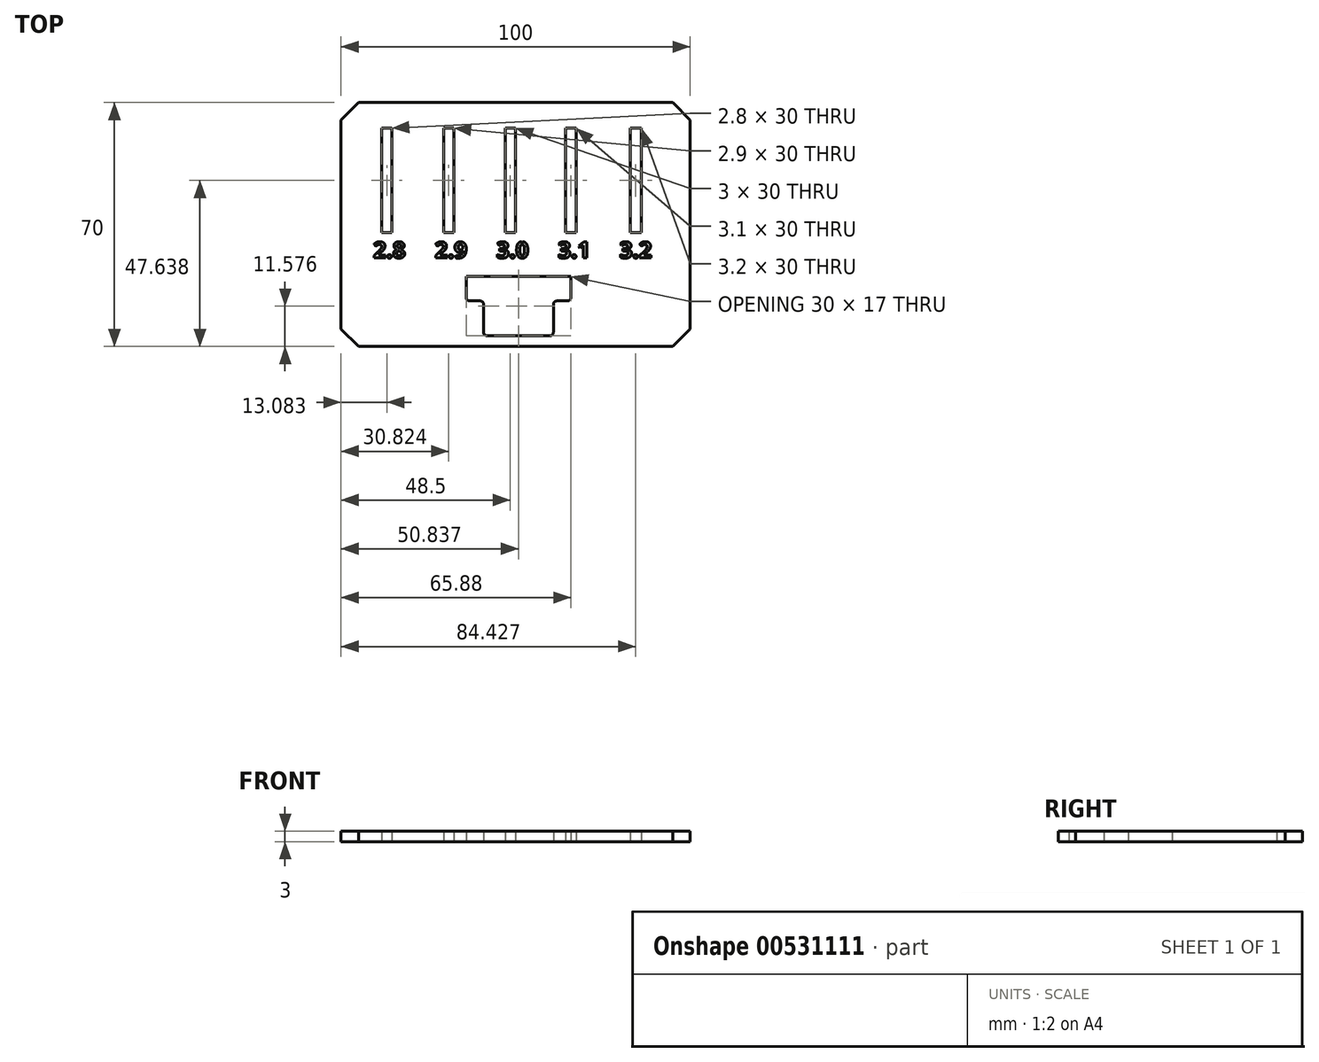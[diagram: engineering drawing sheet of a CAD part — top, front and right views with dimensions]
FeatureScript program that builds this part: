
annotation { "Feature Type Name" : "Feature", "Feature Type Description" : "" }
export const myFeature = defineFeature(function(context is Context, id is Id, definition is map)
    precondition{}
    {
        {
            var Q0;
            Q0=qCreatedBy(makeId("Top.planeOp"),FACE);
            var sketch = newSketch(context, id + "F0", { "sketchPlane" : qUnion([Q0])});
            skLineSegment(sketch, "E0.bottom", {"start": v(50, -35) * mm, "end": v(-50, -35) * mm});
            skLineSegment(sketch, "E0.top", {"start": v(50, 35) * mm, "end": v(-50, 35) * mm});
            skLineSegment(sketch, "E0.left", {"start": v(50, -35) * mm, "end": v(50, 35) * mm});
            skLineSegment(sketch, "E0.right", {"start": v(-50, -35) * mm, "end": v(-50, 35) * mm});
            skPoint(sketch, "E0.middle", {"position": v(1.48, 3.46) * mm});
            skLineSegment(sketch, "E1.bottom", {"start": v(-38.32, 27.64) * mm, "end": v(-35.52, 27.64) * mm});
            skLineSegment(sketch, "E1.top", {"start": v(-38.32, -2.36) * mm, "end": v(-35.52, -2.36) * mm});
            skLineSegment(sketch, "E1.left", {"start": v(-38.32, 27.64) * mm, "end": v(-38.32, -2.36) * mm});
            skLineSegment(sketch, "E1.right", {"start": v(-35.52, 27.64) * mm, "end": v(-35.52, -2.36) * mm});
            skLineSegment(sketch, "E2.bottom", {"start": v(-20.63, 27.64) * mm, "end": v(-17.73, 27.64) * mm});
            skLineSegment(sketch, "E2.top", {"start": v(-20.63, -2.36) * mm, "end": v(-17.73, -2.36) * mm});
            skLineSegment(sketch, "E2.left", {"start": v(-20.63, 27.64) * mm, "end": v(-20.63, -2.36) * mm});
            skLineSegment(sketch, "E2.right", {"start": v(-17.73, 27.64) * mm, "end": v(-17.73, -2.36) * mm});
            skLineSegment(sketch, "E3.bottom", {"start": v(-3, 27.64) * mm, "end": v(0, 27.64) * mm});
            skLineSegment(sketch, "E3.top", {"start": v(-3, -2.36) * mm, "end": v(0, -2.36) * mm});
            skLineSegment(sketch, "E3.left", {"start": v(-3, 27.64) * mm, "end": v(-3, -2.36) * mm});
            skLineSegment(sketch, "E3.right", {"start": v(0, 27.64) * mm, "end": v(0, -2.36) * mm});
            skLineSegment(sketch, "E4.bottom", {"start": v(14.33, 27.64) * mm, "end": v(17.43, 27.64) * mm});
            skLineSegment(sketch, "E4.top", {"start": v(14.33, -2.36) * mm, "end": v(17.43, -2.36) * mm});
            skLineSegment(sketch, "E4.left", {"start": v(14.33, 27.64) * mm, "end": v(14.33, -2.36) * mm});
            skLineSegment(sketch, "E4.right", {"start": v(17.43, 27.64) * mm, "end": v(17.43, -2.36) * mm});
            skLineSegment(sketch, "E5.bottom", {"start": v(32.83, 27.64) * mm, "end": v(36.03, 27.64) * mm});
            skLineSegment(sketch, "E5.top", {"start": v(32.83, -2.36) * mm, "end": v(36.03, -2.36) * mm});
            skLineSegment(sketch, "E5.left", {"start": v(32.83, 27.64) * mm, "end": v(32.83, -2.36) * mm});
            skLineSegment(sketch, "E5.right", {"start": v(36.03, 27.64) * mm, "end": v(36.03, -2.36) * mm});
            skLineSegment(sketch, "E6", {"start": v(-14.16, -14.92) * mm, "end": v(15.84, -14.92) * mm});
            skLineSegment(sketch, "E7", {"start": v(15.84, -14.92) * mm, "end": v(15.84, -20.92) * mm});
            skLineSegment(sketch, "E8", {"start": v(14.84, -21.92) * mm, "end": v(11.84, -21.92) * mm});
            skLineSegment(sketch, "E9", {"start": v(10.84, -22.92) * mm, "end": v(10.84, -30.92) * mm});
            skLineSegment(sketch, "E10", {"start": v(9.84, -31.92) * mm, "end": v(-8.16, -31.92) * mm});
            skLineSegment(sketch, "E11", {"start": v(-9.16, -30.92) * mm, "end": v(-9.16, -22.92) * mm});
            skLineSegment(sketch, "E12", {"start": v(-10.16, -21.92) * mm, "end": v(-13.16, -21.92) * mm});
            skLineSegment(sketch, "E13", {"start": v(-14.16, -20.92) * mm, "end": v(-14.16, -14.92) * mm});
            skPoint(sketch, "E14.visualSharp", {"position": v(15.84, -21.92) * mm});
            skArc(sketch, "E14.filletArc", {"start": v(14.84, -21.92) * mm, "mid": v(15.54, -21.63) * mm, "end": v(15.84, -20.92) * mm});
            skPoint(sketch, "E15.visualSharp", {"position": v(-14.16, -21.92) * mm});
            skArc(sketch, "E15.filletArc", {"start": v(-14.16, -20.92) * mm, "mid": v(-13.87, -21.63) * mm, "end": v(-13.16, -21.92) * mm});
            skPoint(sketch, "E16.visualSharp", {"position": v(-9.16, -21.92) * mm});
            skArc(sketch, "E16.filletArc", {"start": v(-9.16, -22.92) * mm, "mid": v(-9.46, -22.22) * mm, "end": v(-10.16, -21.92) * mm});
            skPoint(sketch, "E17.visualSharp", {"position": v(10.84, -21.92) * mm});
            skArc(sketch, "E17.filletArc", {"start": v(11.84, -21.92) * mm, "mid": v(11.13, -22.22) * mm, "end": v(10.84, -22.92) * mm});
            skPoint(sketch, "E18.visualSharp", {"position": v(10.84, -31.92) * mm});
            skArc(sketch, "E18.filletArc", {"start": v(9.84, -31.92) * mm, "mid": v(10.54, -31.63) * mm, "end": v(10.84, -30.92) * mm});
            skPoint(sketch, "E19.visualSharp", {"position": v(-9.16, -31.92) * mm});
            skArc(sketch, "E19.filletArc", {"start": v(-9.16, -30.92) * mm, "mid": v(-8.87, -31.63) * mm, "end": v(-8.16, -31.92) * mm});
            skSolve(sketch);
        }
        {
            var Q0;
            Q0=makeQuery(id+"F0.imprint","IMPRINT",FACE,{"disambiguationData":[TD([[makeQuery(id+"F0.imprint","IMPRINT",EDGE,{"derivedFrom":sQuery(id+"F0.wireOp",EDGE,"E0.bottom")}),-1.0]])]});
            extrude(context, id + "F1", {"entities" : qUnion([Q0]), "depth" : 3 * mm, "offsetDistance" : 25 * mm});
        }
        {
            var Q0;
            Q0=makeQuery(id+"F1.opExtrude","CAP_FACE",FACE,{"disambiguationData":[OSD([sQuery(id+"F0.wireOp",EDGE,"E0.bottom"),sQuery(id+"F0.wireOp",EDGE,"E0.top"),sQuery(id+"F0.wireOp",EDGE,"E0.left"),sQuery(id+"F0.wireOp",EDGE,"E0.right"),sQuery(id+"F0.wireOp",EDGE,"E1.bottom"),sQuery(id+"F0.wireOp",EDGE,"E1.top"),sQuery(id+"F0.wireOp",EDGE,"E1.left"),sQuery(id+"F0.wireOp",EDGE,"E1.right"),sQuery(id+"F0.wireOp",EDGE,"E2.bottom"),sQuery(id+"F0.wireOp",EDGE,"E2.top"),sQuery(id+"F0.wireOp",EDGE,"E2.left"),sQuery(id+"F0.wireOp",EDGE,"E2.right"),sQuery(id+"F0.wireOp",EDGE,"E3.bottom"),sQuery(id+"F0.wireOp",EDGE,"E3.top"),sQuery(id+"F0.wireOp",EDGE,"E3.left"),sQuery(id+"F0.wireOp",EDGE,"E3.right"),sQuery(id+"F0.wireOp",EDGE,"E4.bottom"),sQuery(id+"F0.wireOp",EDGE,"E4.top"),sQuery(id+"F0.wireOp",EDGE,"E4.left"),sQuery(id+"F0.wireOp",EDGE,"E4.right"),sQuery(id+"F0.wireOp",EDGE,"E5.bottom"),sQuery(id+"F0.wireOp",EDGE,"E5.top"),sQuery(id+"F0.wireOp",EDGE,"E5.left"),sQuery(id+"F0.wireOp",EDGE,"E5.right"),sQuery(id+"F0.wireOp",EDGE,"E6"),sQuery(id+"F0.wireOp",EDGE,"E7"),sQuery(id+"F0.wireOp",EDGE,"E8"),sQuery(id+"F0.wireOp",EDGE,"E9"),sQuery(id+"F0.wireOp",EDGE,"E10"),sQuery(id+"F0.wireOp",EDGE,"E11"),sQuery(id+"F0.wireOp",EDGE,"E12"),sQuery(id+"F0.wireOp",EDGE,"E13"),sQuery(id+"F0.wireOp",EDGE,"E14.filletArc"),sQuery(id+"F0.wireOp",EDGE,"E15.filletArc"),sQuery(id+"F0.wireOp",EDGE,"E16.filletArc"),sQuery(id+"F0.wireOp",EDGE,"E17.filletArc"),sQuery(id+"F0.wireOp",EDGE,"E18.filletArc"),sQuery(id+"F0.wireOp",EDGE,"E19.filletArc")])],"isStart":false});
            var sketch = newSketch(context, id + "F2", { "sketchPlane" : qUnion([Q0])});
            skText(sketch, "E20", { "text": "2.8     2.9     3.0     3.1     3.2", "fontName": "OpenSans-Bold.ttf"});
            const initialGuessF2  = {"E20": [-0.04078, -0.0096, 1, 0, 0.00466]};
            skSetInitialGuess(sketch, initialGuessF2);
            skSolve(sketch);
        }
        {
            var Q0;
            Q0 = qSketchRegion(id + "F2", true);
            extrude(context, id + "F3", {"entities" : qUnion([Q0]), "operationType" : NewBodyOperationType.REMOVE, "oppositeDirection" : true, "depth" : .1 * mm, "offsetDistance" : 25 * mm});
        }
        {
            var Q0;
            Q0=makeQuery(id+"F1.opExtrude","SWEPT_EDGE",EDGE,{"disambiguationData":[OSD([sQuery(id+"F0.wireOp",EDGE,"E0.bottom"),sQuery(id+"F0.wireOp",EDGE,"E0.right")])]});
            var Q1;
            Q1=makeQuery(id+"F1.opExtrude","SWEPT_EDGE",EDGE,{"disambiguationData":[OSD([sQuery(id+"F0.wireOp",EDGE,"E0.bottom"),sQuery(id+"F0.wireOp",EDGE,"E0.left")])]});
            var Q2;
            Q2=makeQuery(id+"F1.opExtrude","SWEPT_EDGE",EDGE,{"disambiguationData":[OSD([sQuery(id+"F0.wireOp",EDGE,"E0.top"),sQuery(id+"F0.wireOp",EDGE,"E0.left")])]});
            var Q3;
            Q3=makeQuery(id+"F1.opExtrude","SWEPT_EDGE",EDGE,{"disambiguationData":[OSD([sQuery(id+"F0.wireOp",EDGE,"E0.top"),sQuery(id+"F0.wireOp",EDGE,"E0.right")])]});
            chamfer(context, id + "F4", {"entities" : qUnion([Q0, Q1, Q2, Q3]), "width" : 5 * mm, "tangentPropagation" : true});
        }
    });
